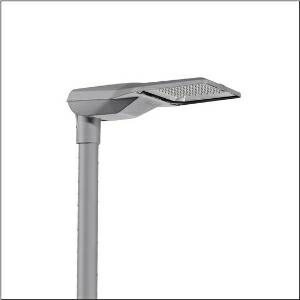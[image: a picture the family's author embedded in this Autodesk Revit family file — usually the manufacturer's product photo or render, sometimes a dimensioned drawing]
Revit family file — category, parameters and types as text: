
# Revit family: streetlight_sl_21_iq_midi___p0_8ab_5xe3r31d08nb_f4a3
name_source: partatom
category: Lighting Fixtures
units: mm (PartAtom-declared; Revit-internal decimal feet)

## family parameters
Cut with Voids When Loaded = No
Host = Face
Light Source = No
Part Type = Normal
Room Calculation Point = No
Round Connector Dimension = Use Diameter
Shared = No

## types (1)
- --- (1 x LED, 20170 lm, 155.5 W, 3000K)
    Apparent Load = 155 VA
    CIE Flux Codes = 39 72 97 100 100
    Color Rendering = 70
    Color Temperature = 3000K
    Default Elevation = 1800 mm
    Description = Streetlight SL 21 iQ midi, mast luminaire, primary light control with lens, of PMMA, primary optical cover: cover, of toughened safety glass, transparent, light distribution: P0.8aB, light emission: direct distribution, primary light characteristic: asymmetric, installation type: post-top, side-entry, LED, High Power LED, rated luminous flux: 20.170lm, luminous efficacy: 130lm/W, light colour: 730, colour temperature: 3000K, control gear: iQ-Comfort, control: pre-setting: linear dimming characteristic, Auto-Match, Temp-Guard, Lumen-Switch, Night-Set, Smart-Wire, Light-Fading, Desk-Remote (wireless, voltage-free reading and setting of iQ features in the workshop via application-optimized NFC function/RFID function), optimised constant luminous flux control (CLO 2.0), mains connection: 230..240V, AC, 50/60Hz, start of lifetime: 156W, end of service life: 162W, reduction: 69W, luminaire housing, of diecast aluminium, powder-coated, SITECO metallic grey (DB 702S), corrosivity category C5 high according to DIN EN ISO 12944, please order mast flange separately, inclination adjustable: 0°, 5°, 10°, 15°, sealing non-destructively replaceable, multi-level sealing system, length: 644mm, width: 335mm, height: 110mm, mast flange for spigot size: 42mm (side-entry): 5XC10008XM4, 60/48mm (side-entry/post-top): 5XC10108XM2, 76/60mm (side-entry/post-top): 5XC10108XM1, mounting height: 4..8m, protection rating (complete): IP66, insulation class (complete): insulation class II (safety insulation), certification: CE, ENEC, ENEC+, VDE, impact resistance: IK10, permissible operating ambient temperature for outdoor applications: -40..+50°C, standard-compliant lighting for roads and squares, packaging unit: 1 piece

Light Distribution: P0.8aB
    Height = 111 mm
    Lamp = 1 x LED
    Lamp Light Flux = 20170 lm
    Lamp Power = 155.5 W
    Lamp count = 1
    Length = 644 mm
    Luminous efficacy = 130 lm/W
    Manufacturer = Siteco
    ModVariant = No
    Model = 5XE3R31D08NB
    Number of Poles = 1
    OnlyDefault = Yes
    Power Factor = 1
    Product Name = Streetlight SL 21 iQ midi | P0.8aB
    Product group = mast luminaire | pylon top
    ProductGroupID = 6100
    Protection Class = Protection class II
    Protection Degree = IP 66
    RLX_Detail_Level = 1
    RLX_Emergency_Light_Flux = 0 lm
    RLX_Emergency_Type = 0
    RLX_Emergency_Type_DB = No
    RlxData = <blob elided: 90441 chars, md5=b87f7213>
    Socket = socket
    Standby Power = 0 W
    System Light Flux = 20170 lm
    System Power = 155 W
    Type Comments = factory setting: luminous flux: 100 % | dim-lin: 254 | 823 mA
    Type Image = l_1004298.jpg
    URL = http://relux.com
    VarID = @adj_078799
    Voltage = 0 V
    Weight = 0.00 kg
    Width = 336 mm

## geometry (parser evidence)
native form markers: Blend x4, Sweep x12
no freeform markers — native parametric forms only
